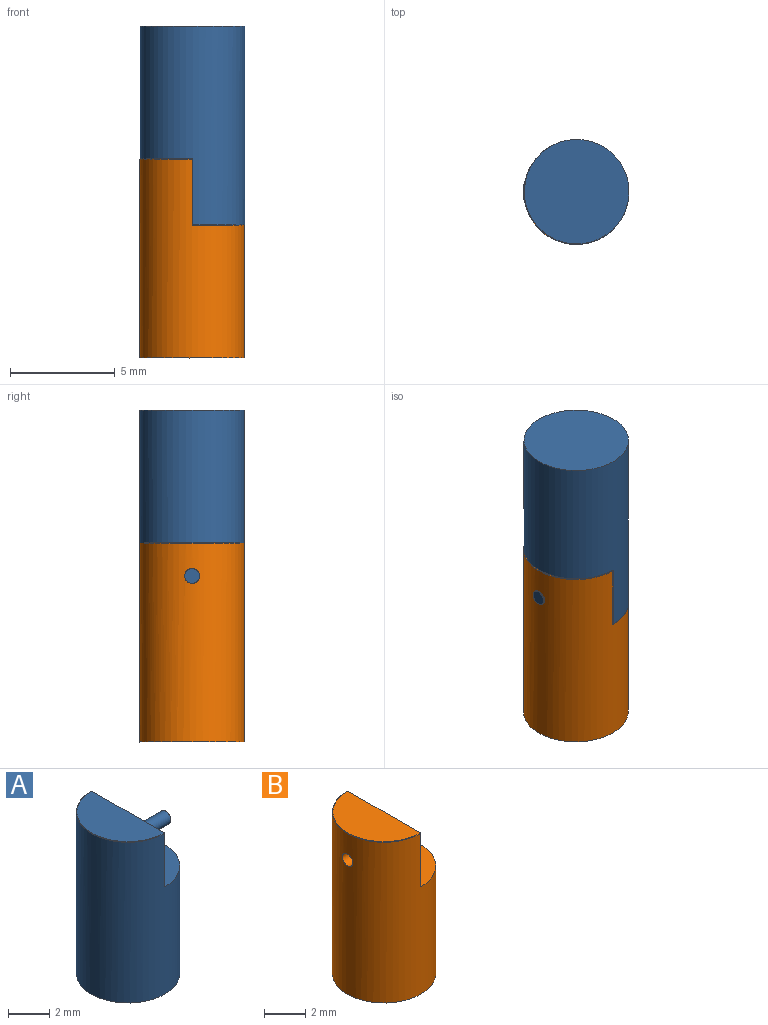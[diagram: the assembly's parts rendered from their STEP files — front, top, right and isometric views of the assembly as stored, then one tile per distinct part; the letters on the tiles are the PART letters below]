
ASSEMBLY  parts=2 mates=1
PART A: 8 faces, bbox 5.3x5.4x9.5 mm
  f0: cylinder r=2.5mm len=9.5mm, axis (0,0,-1), area 124.5mm2, adj f2,f3,f4,f5
  f1: plane 4.95x2.48mm, normal (0,0,1), area 9.6mm2, adj f3,f5
  f2: plane 5x5mm, normal (0,0,-1), area 19.6mm2, adj f0
  f3: plane 5x3.18mm, normal (1,0,0), area 15.5mm2, adj f0,f1,f4,f5,f6
  f4: plane 5x2.5mm, normal (0,0,1), area 9.8mm2, adj f0,f3
  f5: torus R=2.48mm, axis (0,0,1), area 0.3mm2, adj f0,f1,f3
  f6: cylinder r=0.35mm len=2.57mm, axis (-1,0,0), area 5.7mm2, adj f3,f7
  f7: plane 0.71x0.71mm, normal (1,0,0), area 0.4mm2, adj f6
PART B: 7 faces, bbox 5.2x5.4x9.5 mm
  f0: cylinder r=2.5mm len=9.5mm, axis (0,0,-1), area 124.1mm2, adj f2,f3,f4,f5,f6
  f1: plane 4.95x2.48mm, normal (0,0,1), area 9.6mm2, adj f3,f5
  f2: plane 5x5mm, normal (0,0,-1), area 19.6mm2, adj f0
  f3: plane 5x3.18mm, normal (1,0,0), area 15.5mm2, adj f0,f1,f4,f5,f6
  f4: plane 5x2.5mm, normal (0,0,1), area 9.8mm2, adj f0,f3
  f5: torus R=2.48mm, axis (0,0,1), area 0.3mm2, adj f0,f1,f3
  f6: cylinder r=0.35mm len=2.5mm, axis (1,0,0), area 5.5mm2, adj f0,f3
PLACE A rot(axis=(0,1,0),180deg) t=(-8.3,-0.91,14.75)mm
PLACE B rot(axis=(-1,0,0.02),0deg) t=(-8.32,-0.91,-1.13)mm
MATE revolute A.f6 <-> B.f6  axis (1,0,0) through (-9.58,-0.91,6.81)mm
